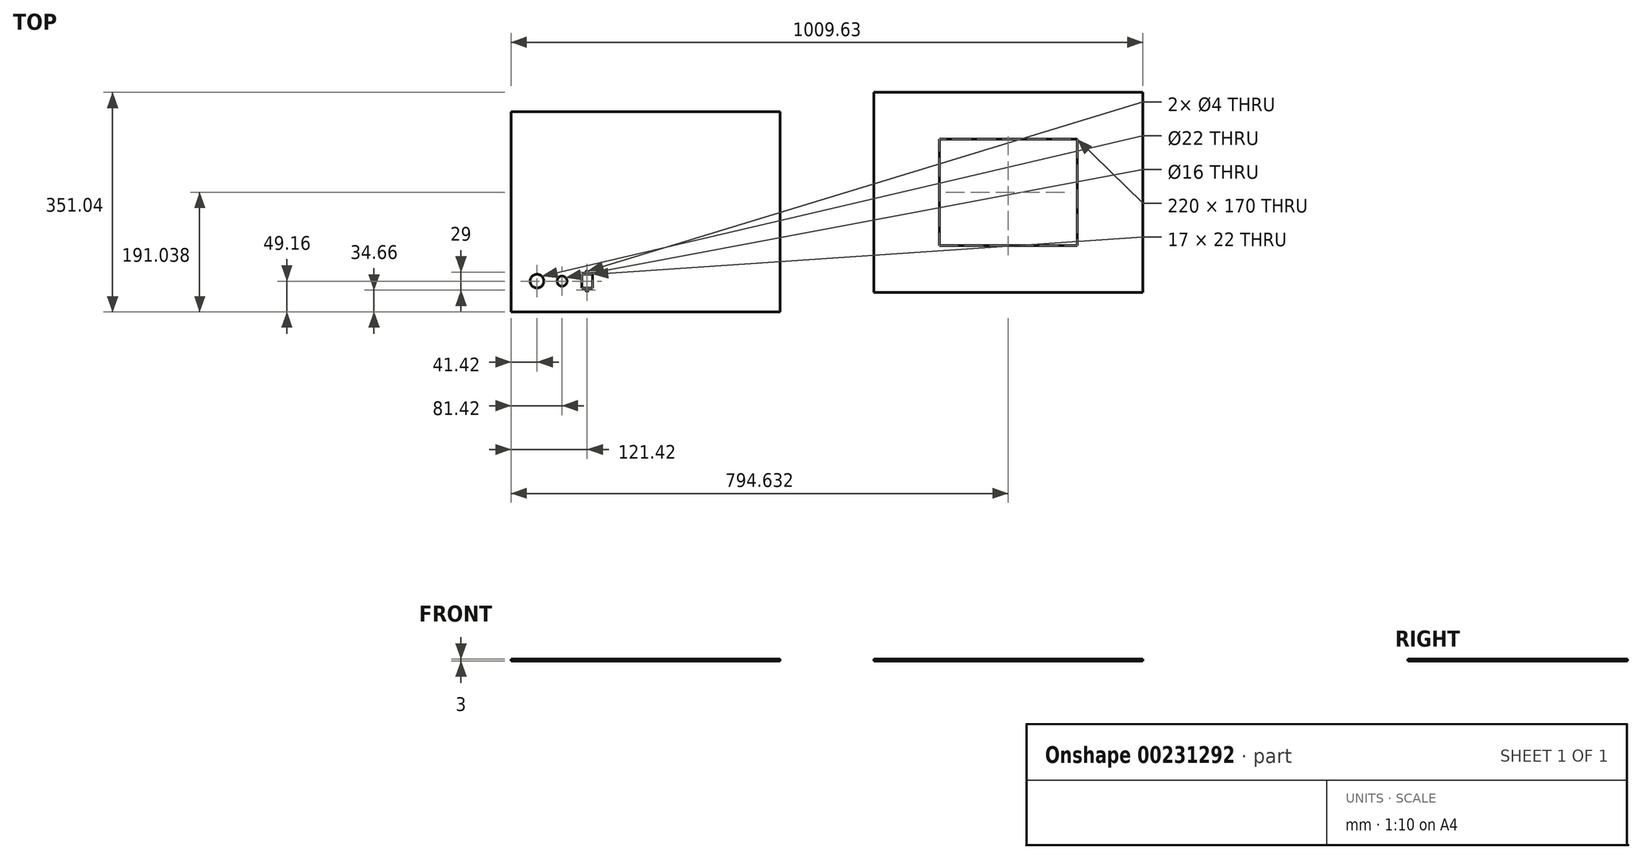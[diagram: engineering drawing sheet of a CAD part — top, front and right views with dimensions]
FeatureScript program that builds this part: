
annotation { "Feature Type Name" : "Feature", "Feature Type Description" : "" }
export const myFeature = defineFeature(function(context is Context, id is Id, definition is map)
    precondition{}
    {
        {
            var Q0;
            Q0=qCreatedBy(makeId("Top.planeOp"),FACE);
            var sketch = newSketch(context, id + "F0", { "sketchPlane" : qUnion([Q0])});
            skCircle(sketch, "E0", {"center": v(-297, 0) * mm, "radius": 11 * mm});
            skCircle(sketch, "E1", {"center": v(-257, 0) * mm, "radius": 8 * mm});
            skLineSegment(sketch, "E2.bottom", {"start": v(-208.5, -11) * mm, "end": v(-225.5, -11) * mm});
            skLineSegment(sketch, "E2.top", {"start": v(-208.5, 11) * mm, "end": v(-225.5, 11) * mm});
            skLineSegment(sketch, "E2.left", {"start": v(-208.5, -11) * mm, "end": v(-208.5, 11) * mm});
            skLineSegment(sketch, "E2.right", {"start": v(-225.5, -11) * mm, "end": v(-225.5, 11) * mm});
            skPoint(sketch, "E2.middle", {"position": v(-217, 0) * mm});
            skCircle(sketch, "E3", {"center": v(-217, 14.5) * mm, "radius": 2 * mm});
            skCircle(sketch, "E4", {"center": v(-217, -14.5) * mm, "radius": 2 * mm});
            skLineSegment(sketch, "E5.bottom", {"start": v(-338.42, 270.84) * mm, "end": v(91.58, 270.84) * mm});
            skLineSegment(sketch, "E5.top", {"start": v(-338.42, -49.16) * mm, "end": v(91.58, -49.16) * mm});
            skLineSegment(sketch, "E5.left", {"start": v(-338.42, 270.84) * mm, "end": v(-338.42, -49.16) * mm});
            skLineSegment(sketch, "E5.right", {"start": v(91.58, 270.84) * mm, "end": v(91.58, -49.16) * mm});
            skLineSegment(sketch, "E6.bottom", {"start": v(241.21, 301.88) * mm, "end": v(671.21, 301.88) * mm});
            skLineSegment(sketch, "E6.top", {"start": v(241.21, -18.12) * mm, "end": v(671.21, -18.12) * mm});
            skLineSegment(sketch, "E6.left", {"start": v(241.21, 301.88) * mm, "end": v(241.21, -18.12) * mm});
            skLineSegment(sketch, "E6.right", {"start": v(671.21, 301.88) * mm, "end": v(671.21, -18.12) * mm});
            skLineSegment(sketch, "E7.bottom", {"start": v(566.21, 56.88) * mm, "end": v(346.21, 56.88) * mm});
            skLineSegment(sketch, "E7.top", {"start": v(566.21, 226.88) * mm, "end": v(346.21, 226.88) * mm});
            skLineSegment(sketch, "E7.left", {"start": v(566.21, 56.88) * mm, "end": v(566.21, 226.88) * mm});
            skLineSegment(sketch, "E7.right", {"start": v(346.21, 56.88) * mm, "end": v(346.21, 226.88) * mm});
            skPoint(sketch, "E7.middle", {"position": v(456.21, 141.88) * mm});
            skPoint(sketch, "E7.middle.positionSnap0", {"position": v(241.21, 141.88) * mm});
            skPoint(sketch, "E7.middle.positionSnap1", {"position": v(456.21, 301.88) * mm});
            skPoint(sketch, "E7.centerSnap0", {"position": v(241.21, 141.88) * mm});
            skPoint(sketch, "E7.centerSnap1", {"position": v(456.21, 301.88) * mm});
            skSolve(sketch);
        }
        {
            var Q0;
            Q0=makeQuery(id+"F0.imprint","IMPRINT",FACE,{"disambiguationData":[TD([[makeQuery(id+"F0.imprint","IMPRINT",EDGE,{"derivedFrom":sQuery(id+"F0.wireOp",EDGE,"E0")}),-1.0]])]});
            extrude(context, id + "F1", {"entities" : qUnion([Q0]), "depth" : 3 * mm});
        }
        {
            var Q0;
            Q0=makeQuery(id+"F0.imprint","IMPRINT",FACE,{"disambiguationData":[TD([[makeQuery(id+"F0.imprint","IMPRINT",EDGE,{"derivedFrom":sQuery(id+"F0.wireOp",EDGE,"E6.bottom")}),-1.0]])]});
            extrude(context, id + "F2", {"entities" : qUnion([Q0]), "depth" : 3 * mm});
        }
    });
